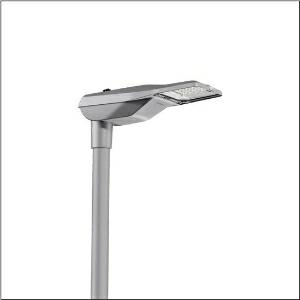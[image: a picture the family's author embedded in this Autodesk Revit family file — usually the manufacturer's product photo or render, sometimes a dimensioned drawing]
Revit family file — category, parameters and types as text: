
# Revit family: streetlight_sl_21_micro___p0_8ab_5xe1r33s08db_200d
name_source: partatom
category: Lighting Fixtures
units: mm (PartAtom-declared; Revit-internal decimal feet)

## family parameters
Cut with Voids When Loaded = No
Host = Face
Light Source = No
Part Type = Normal
Room Calculation Point = No
Round Connector Dimension = Use Diameter
Shared = No

## types (1)
- --- (1 x LED, 4470 lm, 39.1 W, 3000K)
    Apparent Load = 39 VA
    CIE Flux Codes = 36 71 98 100 100
    Color Rendering = 70
    Color Temperature = 3000K
    Default Elevation = 1800 mm
    Description = Streetlight SL 21 micro, mast luminaire, primary light control with lens, of PMMA, primary optical cover: cover, of toughened safety glass, transparent, light distribution: P0.8aB, light emission: direct distribution, primary light characteristic: asymmetric, installation type: post-top, side-entry, LED, High Power LED, rated luminous flux: 4.470lm, luminous efficacy: 114lm/W, light colour: 730, colour temperature: 3000K, control gear: D4i, control: pre-setting: logarithmic dimming characteristic, flexible luminous flux parameterisation, time-dependent luminous flux control, constant luminous flux control, overheat protection, mains connection: 220..240V, AC, 50/60Hz, start of lifetime: 39W, end of service life: 41W, reduction: 18W, luminaire housing, of diecast aluminium, powder-coated, Siteco® metallic grey (DB 702S), corrosivity category C5 mid according to DIN EN ISO 12944, multi-level sealing system, sealing non-destructively replaceable, inclination adjustable: 0°, 5°, 10°, 15°, please order mast flange separately, length: 528mm, width: 235mm, height: 110mm, mast flange for spigot size: 42mm (side-entry): 5XC10008XM4, 60/48mm (side-entry/post-top): 5XC10108XM2, 76/60mm (side-entry/post-top): 5XC10108XM1, Smart Interface above, protection rating (complete): IP66, insulation class (complete): insulation class II (safety insulation), certification: CE, ENEC, ENEC+, VDE, impact resistance: IK09, permissible operating ambient temperature for outdoor applications: -40..+50°C, standard-compliant lighting for roads and squares, packaging unit: 1 piece

Light Distribution: P0.8aB
    Height = 110 mm
    Lamp = 1 x LED
    Lamp Light Flux = 4470 lm
    Lamp Power = 39.1 W
    Lamp count = 1
    Length = 528 mm
    Luminous efficacy = 114 lm/W
    Manufacturer = Siteco
    ModVariant = No
    Model = 5XE1R33S08DB
    Number of Poles = 1
    OnlyDefault = Yes
    Power Factor = 1
    Product Name = Streetlight SL 21 micro | P0.8aB
    Product group = mast luminaire | pylon top
    ProductGroupID = 6100
    Protection Class = Protection class II
    Protection Degree = IP 66
    RLX_Detail_Level = 1
    RLX_Emergency_Light_Flux = 0 lm
    RLX_Emergency_Type = 0
    RLX_Emergency_Type_DB = No
    RlxData = <blob elided: 97901 chars, md5=c6cafbb4>
    Socket = socket
    Standby Power = 0 W
    System Light Flux = 4470 lm
    System Power = 39 W
    Type Comments = factory setting: luminous flux: 100 % | dim-lin: 254 | 765 mA
    Type Image = l_1277292.jpg
    URL = http://relux.com
    VarID = @adj_072270
    Voltage = 0 V
    Weight = 0.00 kg
    Width = 235 mm

## geometry (parser evidence)
native form markers: Blend x4, Sweep x9
no freeform markers — native parametric forms only
